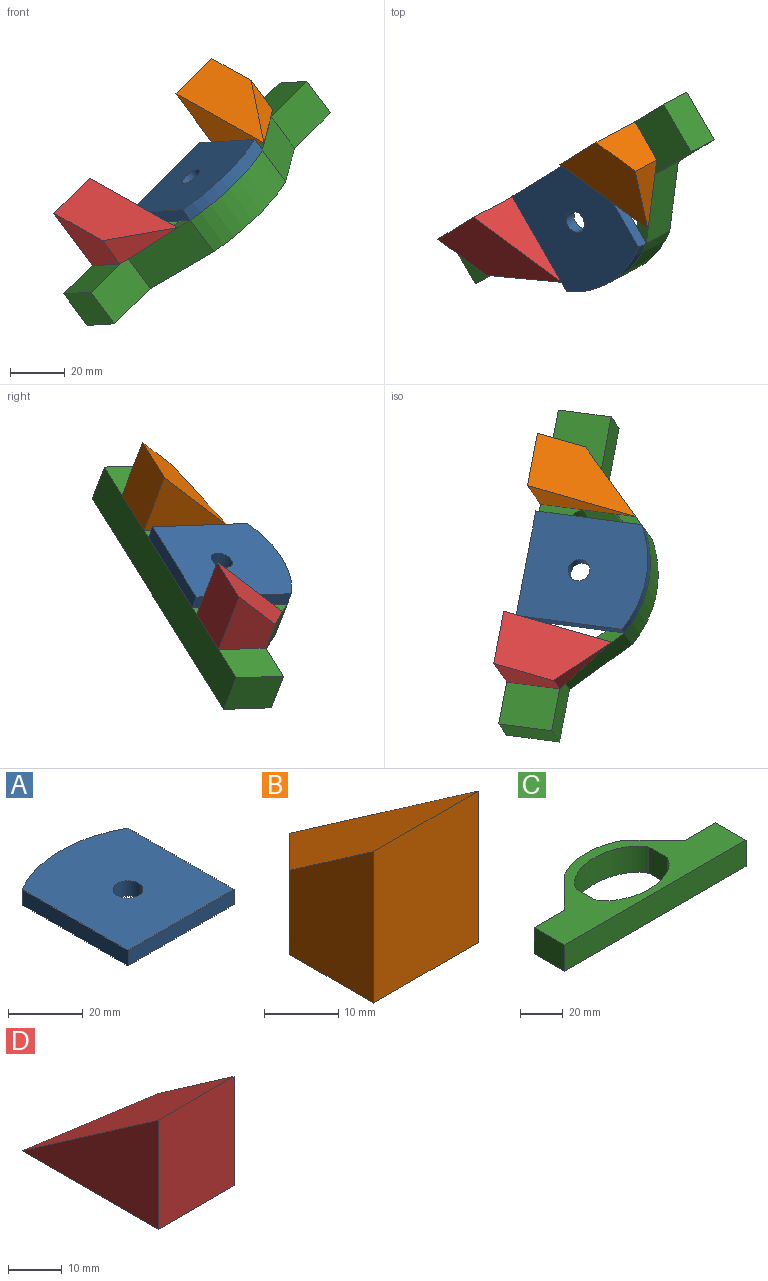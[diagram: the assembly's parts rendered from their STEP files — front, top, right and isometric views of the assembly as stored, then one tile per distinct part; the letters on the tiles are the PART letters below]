
ASSEMBLY  parts=4 mates=8
PART A: 7 faces, bbox 40x45.4x5 mm
  f0: plane 40x5mm, normal (-1,0,0), area 200mm2, adj f1,f4,f5,f6
  f1: plane 40x5mm, normal (0,-1,0), area 200mm2, adj f0,f2,f5,f6
  f2: plane 40x5mm, normal (1,0,0), area 200mm2, adj f1,f4,f5,f6
  f3: cylinder r=4mm len=8mm, axis (0,0,-1), area 125.7mm2, adj f5,f6
  f4: cylinder r=40mm len=40mm, axis (0,0,-1), area 209.4mm2, adj f0,f2,f5,f6
  f5: plane 45.36x40mm, normal (0,0,1), area 1694.7mm2, adj f0,f1,f2,f3,f4
  f6: plane 45.36x40mm, normal (0,0,-1), area 1694.7mm2, adj f0,f1,f2,f3,f4
PART B: 6 faces, bbox 20x36x25 mm
  f0: plane 20x20mm, normal (-0.71,0.71,0), area 196.4mm2, adj f1,f4,f5
  f1: plane 25x16mm, normal (-1,0,0), area 311.1mm2, adj f0,f2,f4,f5
  f2: plane 25x20mm, normal (0,-1,0), area 500mm2, adj f1,f3,f4,f5
  f3: plane 36x25mm, normal (1,0,0), area 450mm2, adj f2,f4,f5
  f4: plane 36x20mm, normal (0,0,-1), area 520mm2, adj f0,f1,f2,f3
  f5: plane 36x25mm, normal (0,0.57,0.82), area 633.1mm2, adj f0,f1,f2,f3
PART C: 14 faces, bbox 120x45.4x15 mm
  f0: plane 20x15mm, normal (0,1,0), area 300mm2, adj f1,f11,f12,f13
  f1: plane 20x20mm, normal (0.71,0.71,0), area 424.3mm2, adj f0,f2,f12,f13
  f2: cylinder r=40mm len=40mm, axis (0,0,-1), area 628.3mm2, adj f1,f3,f12,f13
  f3: plane 20x20mm, normal (-0.71,0.71,0), area 424.3mm2, adj f2,f4,f12,f13
  f4: plane 20x15mm, normal (0,1,0), area 300mm2, adj f3,f5,f12,f13
  f5: plane 20x15mm, normal (-1,0,0), area 300mm2, adj f4,f6,f12,f13
  f6: plane 120x15mm, normal (0,-1,0), area 1800mm2, adj f5,f11,f12,f13
  f7: extruded ~48x15mm, area 842.9mm2, adj f8,f10,f12,f13
  f8: plane 15x12.17mm, normal (1,0,0), area 182.5mm2, adj f7,f9,f12,f13
  f9: extruded ~48x15mm, area 842.9mm2, adj f8,f10,f12,f13
  f10: plane 15x12.17mm, normal (-1,0,0), area 182.5mm2, adj f7,f9,f12,f13
  f11: plane 20x15mm, normal (1,0,0), area 300mm2, adj f0,f6,f12,f13
  f12: plane 120x45.36mm, normal (0,0,1), area 2327.4mm2, adj f0,f1,f2,f3,f4,f5,f6,f7
  f13: plane 120x45.36mm, normal (0,0,-1), area 2327.4mm2, adj f0,f1,f2,f3,f4,f5,f6,f7
PART D: 6 faces, bbox 20x36x25 mm
  f0: plane 36x25mm, normal (-1,0,0), area 450mm2, adj f1,f4,f5
  f1: plane 25x20mm, normal (0,-1,0), area 500mm2, adj f0,f2,f4,f5
  f2: plane 25x20mm, normal (1,0,0), area 361.1mm2, adj f1,f3,f4,f5
  f3: plane 20x16mm, normal (0.62,0.78,0), area 142.3mm2, adj f2,f4,f5
  f4: plane 36x20mm, normal (0,0,-1), area 560mm2, adj f0,f1,f2,f3
  f5: plane 36x25mm, normal (0,0.57,0.82), area 681.8mm2, adj f0,f1,f2,f3
PLACE A rot(axis=(-0.91,-0.25,-0.33),171.5deg) t=(-430.83,-806.14,109.76)mm
PLACE B rot(axis=(0.34,0.08,-0.94),151.3deg) t=(-386.03,-779.05,146.91)mm
PLACE C rot(axis=(-0.91,-0.25,-0.33),171.5deg) t=(-454.22,-820.63,80.3)mm
PLACE D rot(axis=(0.34,0.08,-0.94),151.3deg) t=(-430.62,-806.24,103.36)mm
MATE planar A.f5 <-> C.f13  axis (0.57,0.3,-0.77) through (-403.97,-815.61,119.4)mm
MATE planar D.f1 <-> C.f6  axis (-0.5,0.87,-0.03) through (-444.26,-813.98,106.54)mm
MATE planar D.f4 <-> C.f13  axis (0.57,0.3,-0.77) through (-429.38,-822.32,98)mm
MATE planar B.f4 <-> C.f13  axis (0.57,0.3,-0.77) through (-386.63,-795.38,140.1)mm
MATE planar C.f10 <-> B.f3  axis (-0.66,-0.4,-0.64) through (-383.92,-803.86,129.01)mm
MATE planar B.f2 <-> C.f6  axis (-0.5,0.87,-0.03) through (-399.68,-786.79,150.1)mm
MATE planar D.f0 <-> C.f8  axis (0.66,0.4,0.64) through (-429.36,-819.13,110.12)mm
MATE planar A.f1 <-> C.f6  axis (-0.5,0.87,-0.03) through (-416.3,-797.39,120.65)mm
